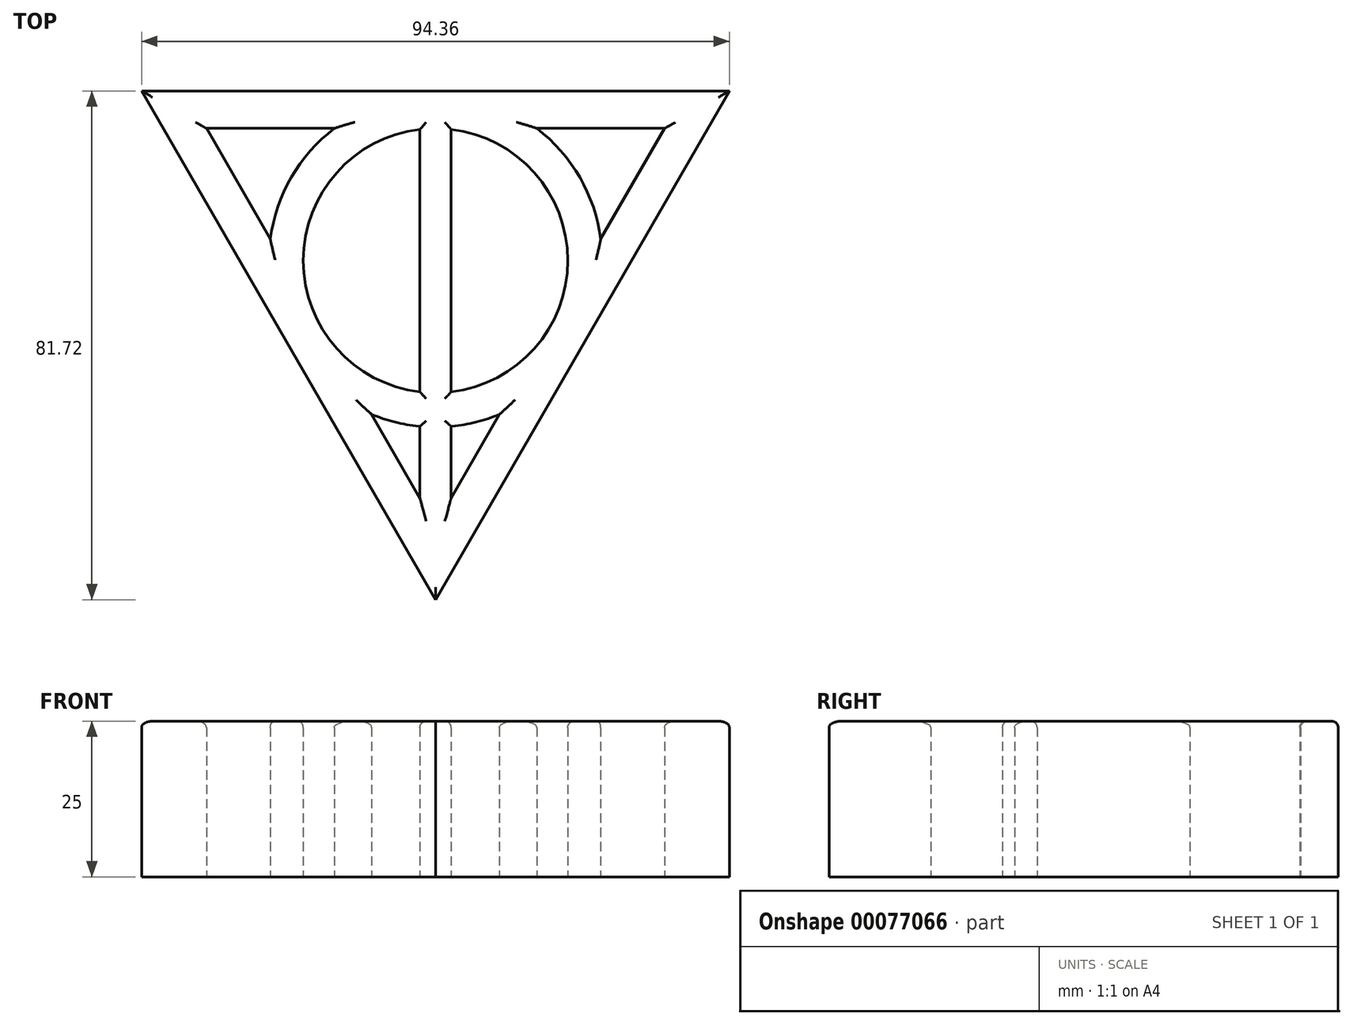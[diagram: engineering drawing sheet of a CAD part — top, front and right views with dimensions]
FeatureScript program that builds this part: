
annotation { "Feature Type Name" : "Feature", "Feature Type Description" : "" }
export const myFeature = defineFeature(function(context is Context, id is Id, definition is map)
    precondition{}
    {
        {
            var Q0;
            Q0=qCreatedBy(makeId("Top.planeOp"),FACE);
            var sketch = newSketch(context, id + "F0", { "sketchPlane" : qUnion([Q0])});
            skPoint(sketch, "E0.0.midPoint", {"position": v(0, 23.24) * mm});
            skLineSegment(sketch, "E1", {"start": v(0, -44.48) * mm, "end": v(0, 23.24) * mm, "construction": true});
            skLineSegment(sketch, "E2.bottom", {"start": v(0, -44.48) * mm, "end": v(0.5, -44.48) * mm});
            skLineSegment(sketch, "E2.top", {"start": v(0, 23.24) * mm, "end": v(0.5, 23.24) * mm});
            skLineSegment(sketch, "E3", {"start": v(0, -42.48) * mm, "end": v(0, 26.5) * mm, "construction": true});
            skLineSegment(sketch, "E4.0", {"start": v(-2.5, -38.15) * mm, "end": v(-10.27, -24.7) * mm});
            skLineSegment(sketch, "E4.1", {"start": v(36.79, 21.24) * mm, "end": v(26.52, 3.46) * mm});
            skLineSegment(sketch, "E4.2", {"start": v(-36.79, 21.24) * mm, "end": v(-16.25, 21.24) * mm});
            skArc(sketch, "E5.0", {"start": v(2.5, -21.1) * mm, "mid": v(21.24, 0) * mm, "end": v(2.5, 21.1) * mm});
            skLineSegment(sketch, "E6.trimOffspring", {"start": v(-26.52, 3.46) * mm, "end": v(-36.79, 21.24) * mm});
            skLineSegment(sketch, "E7.trimOffspring", {"start": v(-2.5, -21.1) * mm, "end": v(-2.5, 21.24) * mm});
            skLineSegment(sketch, "E8.trimOffspring", {"start": v(2.5, -21.1) * mm, "end": v(2.5, 21.24) * mm});
            skPoint(sketch, "E9.orphan", {"position": v(0, -47.56) * mm});
            skLineSegment(sketch, "E10.trimOffspring", {"start": v(10.27, -24.7) * mm, "end": v(2.5, -38.15) * mm});
            skLineSegment(sketch, "E11.trimOffspring", {"start": v(16.25, 21.24) * mm, "end": v(36.79, 21.24) * mm});
            skArc(sketch, "E12.trimOffspring", {"start": v(0.52, 25.24) * mm, "mid": v(0, 25.24) * mm, "end": v(-0.52, 25.24) * mm});
            skArc(sketch, "E13.trimOffspring", {"start": v(-2.5, 21.1) * mm, "mid": v(-21.24, 0) * mm, "end": v(-2.5, -21.1) * mm});
            skLineSegment(sketch, "E14", {"start": v(-2.5, -26.63) * mm, "end": v(-2.5, -38.15) * mm});
            skLineSegment(sketch, "E15", {"start": v(2.5, -26.63) * mm, "end": v(2.5, -38.15) * mm});
            skLineSegment(sketch, "E16.0", {"start": v(-47.18, 27.24) * mm, "end": v(47.18, 27.24) * mm});
            skLineSegment(sketch, "E16.1", {"start": v(0, -54.48) * mm, "end": v(-47.18, 27.24) * mm});
            skLineSegment(sketch, "E16.2", {"start": v(47.18, 27.24) * mm, "end": v(0, -54.48) * mm});
            skArc(sketch, "E17.0", {"start": v(-16.25, 21.24) * mm, "mid": v(-23.16, 13.37) * mm, "end": v(-26.52, 3.46) * mm});
            skArc(sketch, "E18.0", {"start": v(26.52, 3.46) * mm, "mid": v(23.16, 13.37) * mm, "end": v(16.25, 21.24) * mm});
            skArc(sketch, "E19.0", {"start": v(2.65, -26.61) * mm, "mid": v(6.53, -25.93) * mm, "end": v(10.27, -24.7) * mm});
            skLineSegment(sketch, "E20", {"start": v(2.65, -26.61) * mm, "end": v(2.5, -26.63) * mm});
            skArc(sketch, "E21.0", {"start": v(-10.27, -24.7) * mm, "mid": v(-6.53, -25.93) * mm, "end": v(-2.65, -26.61) * mm});
            skLineSegment(sketch, "E22", {"start": v(-2.65, -26.61) * mm, "end": v(-2.5, -26.63) * mm});
            skSolve(sketch);
        }
        {
            var Q0;
            Q0 = qSketchRegion(id + "F0", true);
            extrude(context, id + "F1", {"entities" : qUnion([Q0]), "depth" : 25 * mm});
        }
        {
            var Q0;
            Q0=makeQuery(id+"F1.opExtrude","CAP_EDGE",EDGE,{"disambiguationData":[OSD([sQuery(id+"F0.wireOp",EDGE,"E16.1")])],"isStart":false});
            var Q1;
            Q1=makeQuery(id+"F1.opExtrude","CAP_EDGE",EDGE,{"disambiguationData":[OSD([sQuery(id+"F0.wireOp",EDGE,"E16.0")])],"isStart":false});
            var Q2;
            Q2=makeQuery(id+"F1.opExtrude","CAP_EDGE",EDGE,{"disambiguationData":[OSD([sQuery(id+"F0.wireOp",EDGE,"E16.2")])],"isStart":false});
            fillet(context, id + "F2", {"entities" : qUnion([Q0, Q1, Q2]), "radius" : 1 * mm, "tangentPropagation" : true, "allowEdgeOverflow" : false});
        }
        {
            var Q0;
            Q0=makeQuery(id+"F1.opExtrude","CAP_EDGE",EDGE,{"disambiguationData":[OSD([sQuery(id+"F0.wireOp",EDGE,"E4.0")])],"isStart":false});
            var Q1;
            Q1=makeQuery(id+"F1.opExtrude","CAP_EDGE",EDGE,{"disambiguationData":[OSD([sQuery(id+"F0.wireOp",EDGE,"E21.0")])],"isStart":false});
            var Q2;
            Q2=makeQuery(id+"F1.opExtrude","CAP_EDGE",EDGE,{"disambiguationData":[OSD([sQuery(id+"F0.wireOp",EDGE,"E14")])],"isStart":false});
            var Q3;
            Q3=makeQuery(id+"F1.opExtrude","CAP_EDGE",EDGE,{"disambiguationData":[OSD([sQuery(id+"F0.wireOp",EDGE,"E15")])],"isStart":false});
            var Q4;
            Q4=makeQuery(id+"F1.opExtrude","CAP_EDGE",EDGE,{"disambiguationData":[OSD([sQuery(id+"F0.wireOp",EDGE,"E19.0")])],"isStart":false});
            var Q5;
            Q5=makeQuery(id+"F1.opExtrude","CAP_EDGE",EDGE,{"disambiguationData":[OSD([sQuery(id+"F0.wireOp",EDGE,"E10.trimOffspring")])],"isStart":false});
            var Q6;
            Q6=makeQuery(id+"F1.opExtrude","CAP_EDGE",EDGE,{"disambiguationData":[OSD([sQuery(id+"F0.wireOp",EDGE,"E5.0")])],"isStart":false});
            var Q7;
            Q7=makeQuery(id+"F1.opExtrude","CAP_EDGE",EDGE,{"disambiguationData":[OSD([sQuery(id+"F0.wireOp",EDGE,"E8.trimOffspring")])],"isStart":false});
            var Q8;
            Q8=makeQuery(id+"F1.opExtrude","CAP_EDGE",EDGE,{"disambiguationData":[OSD([sQuery(id+"F0.wireOp",EDGE,"E7.trimOffspring")])],"isStart":false});
            var Q9;
            Q9=makeQuery(id+"F1.opExtrude","CAP_EDGE",EDGE,{"disambiguationData":[OSD([sQuery(id+"F0.wireOp",EDGE,"E13.trimOffspring")])],"isStart":false});
            var Q10;
            Q10=makeQuery(id+"F1.opExtrude","CAP_EDGE",EDGE,{"disambiguationData":[OSD([sQuery(id+"F0.wireOp",EDGE,"E17.0")])],"isStart":false});
            var Q11;
            Q11=makeQuery(id+"F1.opExtrude","CAP_EDGE",EDGE,{"disambiguationData":[OSD([sQuery(id+"F0.wireOp",EDGE,"E6.trimOffspring")])],"isStart":false});
            var Q12;
            Q12=makeQuery(id+"F1.opExtrude","CAP_EDGE",EDGE,{"disambiguationData":[OSD([sQuery(id+"F0.wireOp",EDGE,"E4.2")])],"isStart":false});
            var Q13;
            Q13=makeQuery(id+"F1.opExtrude","CAP_EDGE",EDGE,{"disambiguationData":[OSD([sQuery(id+"F0.wireOp",EDGE,"E11.trimOffspring")])],"isStart":false});
            var Q14;
            Q14=makeQuery(id+"F1.opExtrude","CAP_EDGE",EDGE,{"disambiguationData":[OSD([sQuery(id+"F0.wireOp",EDGE,"E4.1")])],"isStart":false});
            var Q15;
            Q15=makeQuery(id+"F1.opExtrude","CAP_EDGE",EDGE,{"disambiguationData":[OSD([sQuery(id+"F0.wireOp",EDGE,"E18.0")])],"isStart":false});
            fillet(context, id + "F3", {"entities" : qUnion([Q0, Q1, Q2, Q3, Q4, Q5, Q6, Q7, Q8, Q9, Q10, Q11, Q12, Q13, Q14, Q15]), "radius" : 1 * mm, "tangentPropagation" : true, "allowEdgeOverflow" : false});
        }
    });
